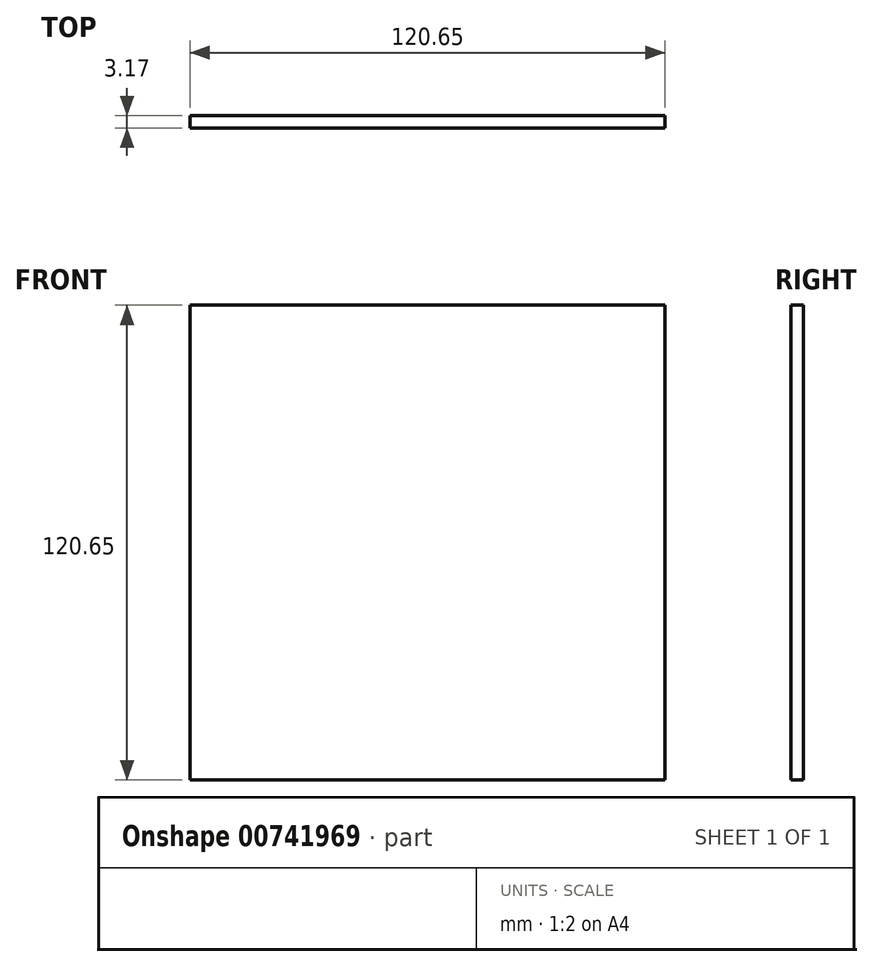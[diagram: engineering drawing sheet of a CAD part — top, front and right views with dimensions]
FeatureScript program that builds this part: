
annotation { "Feature Type Name" : "Feature", "Feature Type Description" : "" }
export const myFeature = defineFeature(function(context is Context, id is Id, definition is map)
    precondition{}
    {
        {
            var Q0;
            Q0=qCreatedBy(makeId("Front.planeOp"),FACE);
            var sketch = newSketch(context, id + "F0", { "sketchPlane" : qUnion([Q0])});
            skLineSegment(sketch, "E0.bottom", {"start": v(-41.12, 82.4) * mm, "end": v(79.53, 82.4) * mm});
            skLineSegment(sketch, "E0.top", {"start": v(-41.12, -38.26) * mm, "end": v(79.53, -38.26) * mm});
            skLineSegment(sketch, "E0.left", {"start": v(-41.12, 82.4) * mm, "end": v(-41.12, -38.26) * mm});
            skLineSegment(sketch, "E0.right", {"start": v(79.53, 82.4) * mm, "end": v(79.53, -38.26) * mm});
            skSolve(sketch);
        }
        {
            var Q0;
            Q0 = qSketchRegion(id + "F0", true);
            extrude(context, id + "F1", {"entities" : qUnion([Q0]), "depth" : 3.17 * mm, "offsetDistance" : 25.4 * mm});
        }
    });
